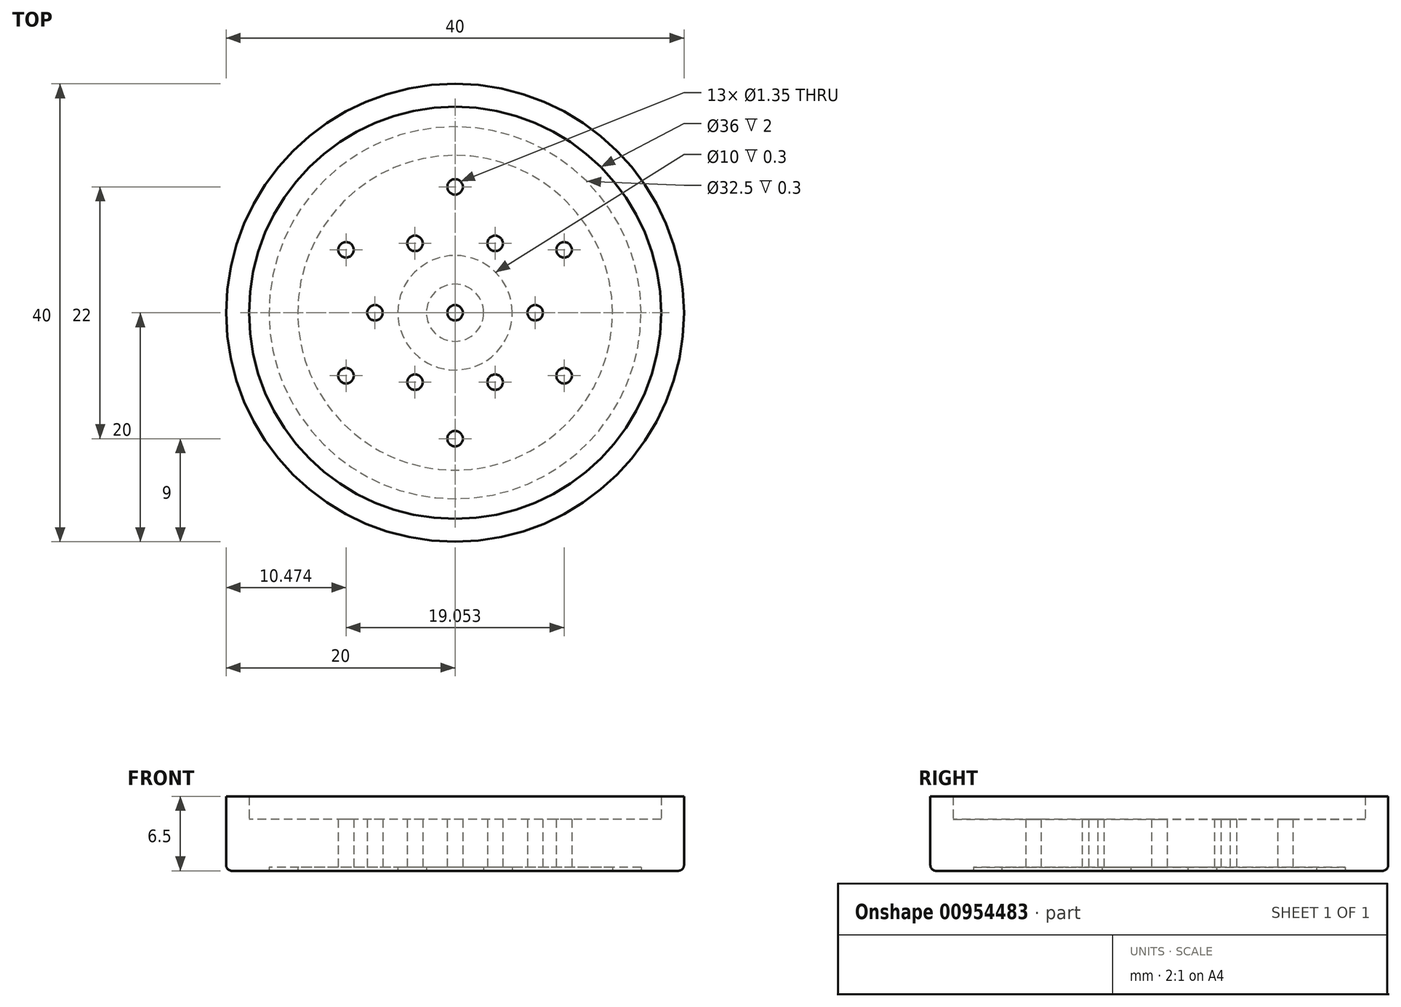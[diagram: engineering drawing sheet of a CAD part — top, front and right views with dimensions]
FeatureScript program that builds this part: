
annotation { "Feature Type Name" : "Feature", "Feature Type Description" : "" }
export const myFeature = defineFeature(function(context is Context, id is Id, definition is map)
    precondition{}
    {
        {
            var Q0;
            Q0=qCreatedBy(makeId("Top.planeOp"),FACE);
            var sketch = newSketch(context, id + "F0", { "sketchPlane" : qUnion([Q0])});
            skCircle(sketch, "E0", {"center": v(0, 0) * mm, "radius": 20 * mm});
            skCircle(sketch, "E1", {"center": v(0, 11) * mm, "radius": 0.68 * mm});
            skCircle(sketch, "E2.1.0", {"center": v(-9.53, 5.5) * mm, "radius": 0.68 * mm});
            skCircle(sketch, "E2.2.0", {"center": v(-9.53, -5.5) * mm, "radius": 0.68 * mm});
            skCircle(sketch, "E2.3.0", {"center": v(0, -11) * mm, "radius": 0.68 * mm});
            skCircle(sketch, "E2.4.0", {"center": v(9.53, -5.5) * mm, "radius": 0.68 * mm});
            skCircle(sketch, "E2.5.0", {"center": v(9.53, 5.5) * mm, "radius": 0.68 * mm});
            skLineSegment(sketch, "E3", {"start": v(0, 0) * mm, "end": v(0, 16.65) * mm, "construction": true});
            skLineSegment(sketch, "E4", {"start": v(0, 0) * mm, "end": v(0, -7.27) * mm, "construction": true});
            skSolve(sketch);
        }
        {
            var Q0;
            Q0=makeQuery(id+"F0.imprint","IMPRINT",FACE,{"disambiguationData":[TD([[makeQuery(id+"F0.imprint","IMPRINT",EDGE,{"derivedFrom":sQuery(id+"F0.wireOp",EDGE,"E0")}),1.0]])]});
            var sketch = newSketch(context, id + "F1", { "sketchPlane" : qUnion([Q0])});
            skPoint(sketch, "E5", {"position": v(-7, 0) * mm});
            skCircle(sketch, "E6", {"center": v(-7, 0) * mm, "radius": 0.67 * mm});
            skCircle(sketch, "E7.1.0", {"center": v(-3.5, -6.06) * mm, "radius": 0.67 * mm});
            skCircle(sketch, "E7.2.0", {"center": v(3.5, -6.06) * mm, "radius": 0.67 * mm});
            skCircle(sketch, "E7.3.0", {"center": v(7, 0) * mm, "radius": 0.67 * mm});
            skCircle(sketch, "E7.4.0", {"center": v(3.5, 6.06) * mm, "radius": 0.67 * mm});
            skCircle(sketch, "E7.5.0", {"center": v(-3.5, 6.06) * mm, "radius": 0.67 * mm});
            skPoint(sketch, "E7.center", {"position": v(0, 0) * mm});
            skCircle(sketch, "E8", {"center": v(0, 0) * mm, "radius": 0.68 * mm});
            skSolve(sketch);
        }
        {
            var Q0;
            Q0=makeQuery(id+"F1.imprint","IMPRINT",FACE,{"disambiguationData":[TD([[makeQuery(id+"F1.imprint","IMPRINT",EDGE,{"derivedFrom":sQuery(id+"F1.wireOp",EDGE,"E6")}),-1.0]])]});
            extrude(context, id + "F2", {"entities" : qUnion([Q0]), "depth" : 4.5 * mm, "offsetDistance" : 25 * mm});
        }
        {
            var Q0;
            Q0=makeQuery(id+"F2.opExtrude","CAP_FACE",FACE,{"disambiguationData":[OSD([sQuery(id+"F0.wireOp",EDGE,"E0"),sQuery(id+"F0.wireOp",EDGE,"E1"),sQuery(id+"F0.wireOp",EDGE,"E2.1.0"),sQuery(id+"F0.wireOp",EDGE,"E2.2.0"),sQuery(id+"F0.wireOp",EDGE,"E2.3.0"),sQuery(id+"F0.wireOp",EDGE,"E2.4.0"),sQuery(id+"F0.wireOp",EDGE,"E2.5.0"),sQuery(id+"F1.wireOp",EDGE,"E6"),sQuery(id+"F1.wireOp",EDGE,"E7.1.0"),sQuery(id+"F1.wireOp",EDGE,"E7.2.0"),sQuery(id+"F1.wireOp",EDGE,"E7.3.0"),sQuery(id+"F1.wireOp",EDGE,"E7.4.0"),sQuery(id+"F1.wireOp",EDGE,"E7.5.0"),sQuery(id+"F1.wireOp",EDGE,"E8")])],"isStart":false});
            var sketch = newSketch(context, id + "F3", { "sketchPlane" : qUnion([Q0])});
            skCircle(sketch, "E9", {"center": v(0, 0) * mm, "radius": 20 * mm});
            skCircle(sketch, "E10", {"center": v(0, 0) * mm, "radius": 18 * mm});
            skSolve(sketch);
        }
        {
            var Q0;
            Q0=makeQuery(id+"F3.imprint","IMPRINT",FACE,{"disambiguationData":[TD([[makeQuery(id+"F3.imprint","IMPRINT",EDGE,{"derivedFrom":sQuery(id+"F3.wireOp",EDGE,"E9")}),1.0]])]});
            extrude(context, id + "F4", {"entities" : qUnion([Q0]), "operationType" : NewBodyOperationType.ADD, "depth" : 2 * mm, "offsetDistance" : 25 * mm});
        }
        {
            var Q0;
            Q0=makeQuery(id+"F0.imprint","IMPRINT",FACE,{"disambiguationData":[TD([[makeQuery(id+"F0.imprint","IMPRINT",EDGE,{"derivedFrom":sQuery(id+"F0.wireOp",EDGE,"E0")}),1.0]])]});
            var sketch = newSketch(context, id + "F5", { "sketchPlane" : qUnion([Q0])});
            skCircle(sketch, "E11", {"center": v(0, 0) * mm, "radius": 13.75 * mm});
            skCircle(sketch, "E12", {"center": v(0, 0) * mm, "radius": 16.25 * mm});
            skCircle(sketch, "E13", {"center": v(0, 0) * mm, "radius": 5 * mm});
            skCircle(sketch, "E14", {"center": v(0, 0) * mm, "radius": 2.5 * mm});
            skSolve(sketch);
        }
        {
            var Q0;
            Q0=makeQuery(id+"F5.imprint","IMPRINT",FACE,{"disambiguationData":[TD([[makeQuery(id+"F5.imprint","IMPRINT",EDGE,{"derivedFrom":sQuery(id+"F5.wireOp",EDGE,"E13")}),1.0]])]});
            var Q1;
            Q1=makeQuery(id+"F5.imprint","IMPRINT",FACE,{"disambiguationData":[TD([[makeQuery(id+"F5.imprint","IMPRINT",EDGE,{"derivedFrom":sQuery(id+"F5.wireOp",EDGE,"E11")}),-1.0]])]});
            extrude(context, id + "F6", {"entities" : qUnion([Q0, Q1]), "operationType" : NewBodyOperationType.REMOVE, "depth" : 0.3 * mm, "offsetDistance" : 25 * mm});
        }
        {
            var Q0;
            Q0=makeQuery(id+"F2.opExtrude","CAP_EDGE",EDGE,{"disambiguationData":[OSD([sQuery(id+"F0.wireOp",EDGE,"E0")])],"isStart":true});
            fillet(context, id + "F7", {"entities" : qUnion([Q0]), "tangentPropagation" : true, "radius" : 0.5 * mm, "defaultsChanged" : true, "vertexSettings" : [], "allowEdgeOverflow" : false});
        }
    });
